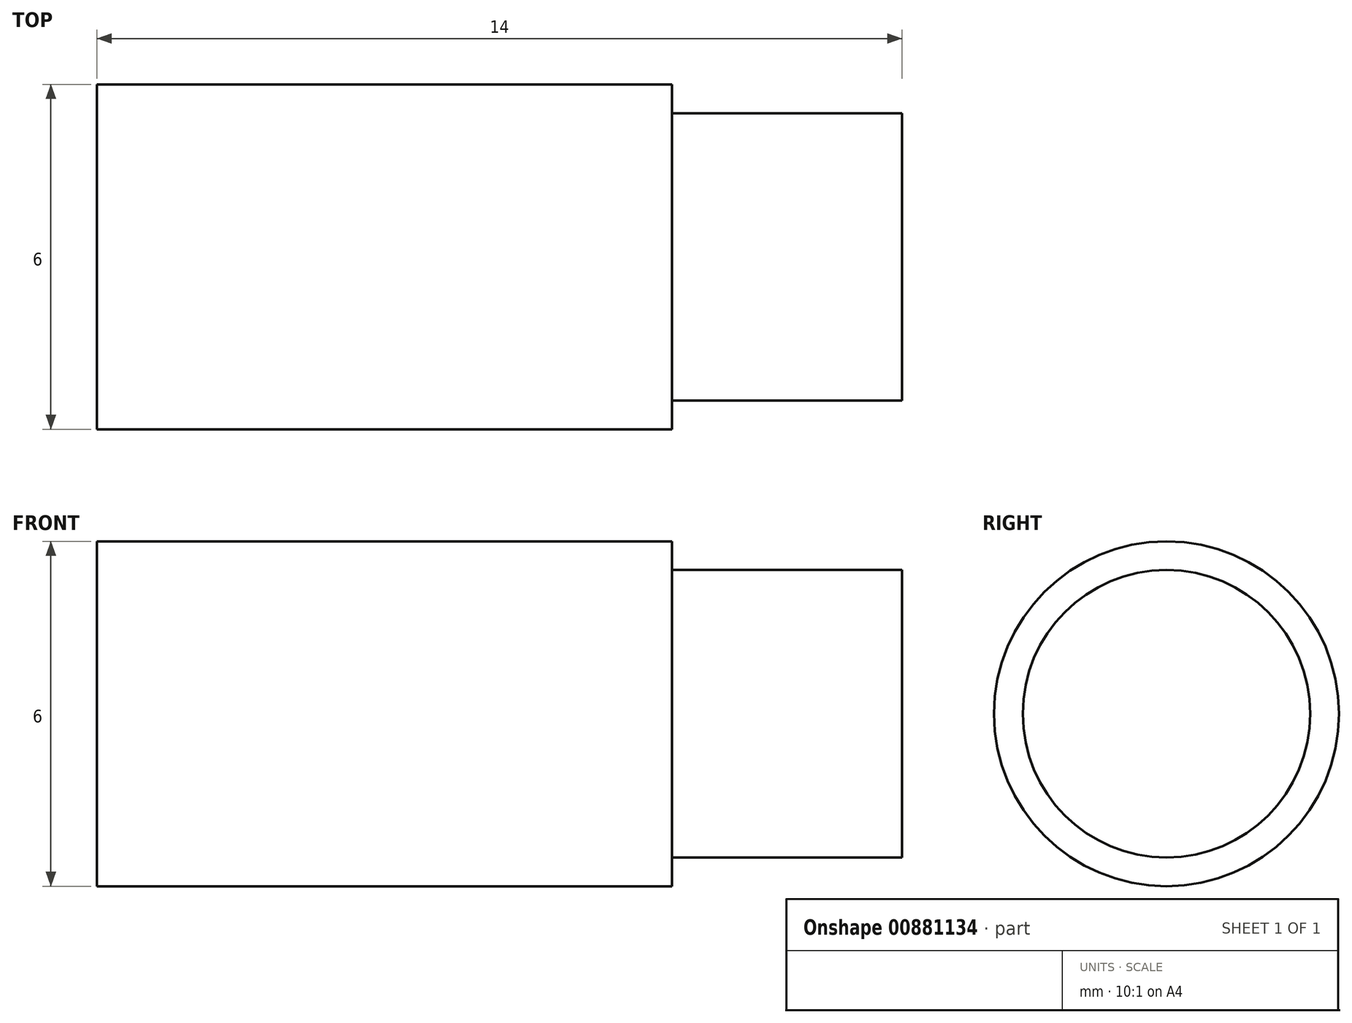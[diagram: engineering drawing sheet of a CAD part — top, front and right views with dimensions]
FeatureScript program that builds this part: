
annotation { "Feature Type Name" : "Feature", "Feature Type Description" : "" }
export const myFeature = defineFeature(function(context is Context, id is Id, definition is map)
    precondition{}
    {
        {
            var Q0;
            Q0=qCreatedBy(makeId("Front.planeOp"),FACE);
            var sketch = newSketch(context, id + "F0", { "sketchPlane" : qUnion([Q0])});
            skLineSegment(sketch, "E0", {"start": v(0, 0) * mm, "end": v(0, 3) * mm});
            skLineSegment(sketch, "E1", {"start": v(0, 3) * mm, "end": v(10, 3) * mm});
            skLineSegment(sketch, "E2", {"start": v(10, 3) * mm, "end": v(10, 2.5) * mm});
            skLineSegment(sketch, "E3", {"start": v(10, 2.5) * mm, "end": v(14, 2.5) * mm});
            skLineSegment(sketch, "E4", {"start": v(14, 2.5) * mm, "end": v(14, 0) * mm});
            skLineSegment(sketch, "E5", {"start": v(14, 0) * mm, "end": v(0, 0) * mm});
            skSolve(sketch);
        }
        {
            var Q0;
            Q0=makeQuery(id+"F0.imprint","IMPRINT",FACE,{"disambiguationData":[TD([[makeQuery(id+"F0.imprint","IMPRINT",EDGE,{"derivedFrom":sQuery(id+"F0.wireOp",EDGE,"E0")}),-1.0]])]});
            var Q1;
            Q1=sQuery(id+"F0.wireOp",EDGE,"E5");
            revolve(context, id + "F1", {"surfaceOperationType" : NewSurfaceOperationType.NEW, "entities" : qUnion([Q0]), "axis" : qUnion([Q1]), "revolveType" : RevolveType.FULL});
        }
    });
